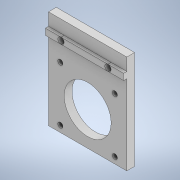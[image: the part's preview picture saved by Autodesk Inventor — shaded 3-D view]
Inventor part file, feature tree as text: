
AUTODESK INVENTOR PART (.ipt)
format: ipt  version: 2021 (Build 250183000, 183)  size: 174,592 bytes
history: native  units: mm
features: extrude x3, sketch x3, projected_geometry x2
ambient origin geometry x8: Origin, YZ Plane, XZ Plane, XY Plane, X Axis, Y Axis, Z Axis, Center Point
bodies: Solid1 (feature_tree)
feature tree (8):
  extrude  "Extrusion1"  Depth=126.0mm
  extrude  "Extrusion2"  Depth=43.0mm
  extrude  "Extrusion3"  Depth=8.0mm
  sketch  "Sketch1"  dims[d0=100.0mm d1=126.0mm]
  sketch  "Sketch2"  dims[d2=60.0mm d3=43.0mm]
  projected_geometry  "Projected Loop1"
  sketch  "Sketch3"  dims[d4=8.0mm d5=8.0mm d6=20.0mm d7=20.0mm d8=20.0mm d9=20.0mm d10=6.5mm d11=6.5mm d12=6.5mm d13=6.5mm d14=69.6mm d15=69.6mm d16=69.6mm d17=69.6mm d18=0.0mm d19=0.0mm d20=34.8mm d21=34.8mm d22=29.0mm d23=20.0mm d24=0.0mm d25=4.0mm d26=4.0mm d27=4.0mm d28=0.0mm d29=6.0mm d30=0.0mm]
  projected_geometry  "Projected Loop2"
